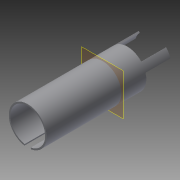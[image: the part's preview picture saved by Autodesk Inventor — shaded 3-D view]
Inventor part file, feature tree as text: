
AUTODESK INVENTOR PART (.ipt)
format: ipt  version: 2013 (Build 170138000, 138)  size: 115,712 bytes
history: native  units: mm
features: extrude x4, sketch x4, other x2
ambient origin geometry x8: Origin, YZ Plane, XZ Plane, XY Plane, X Axis, Y Axis, Z Axis, Center Point
feature tree (10):
  other  "ソリッド1"
  extrude  "押し出し1"  Depth=70.0mm
  extrude  "押し出し3"  Depth=76.0mm
  other  "作業平面2"
  extrude  "押し出し4"  Depth=250.0mm TaperAngle=0.0deg
  extrude  "押し出し5"  Depth=50.0mm TaperAngle=0.0deg
  sketch  "スケッチ1"
  sketch  "スケッチ2"
  sketch  "スケッチ3"
  sketch  "スケッチ4"
